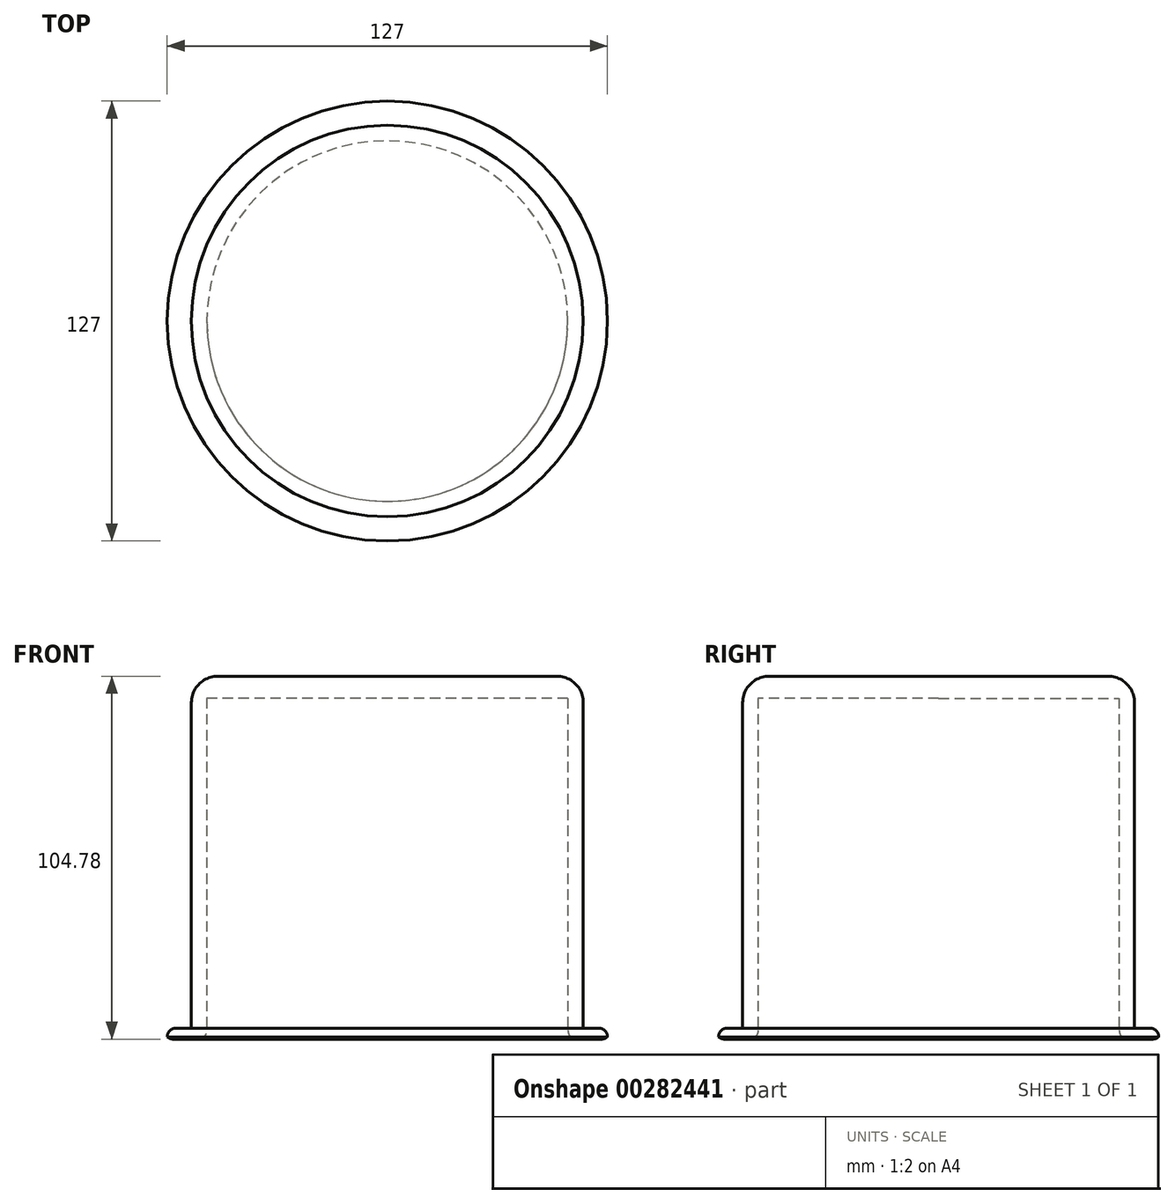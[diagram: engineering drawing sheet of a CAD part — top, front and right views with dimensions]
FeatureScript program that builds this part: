
annotation { "Feature Type Name" : "Feature", "Feature Type Description" : "" }
export const myFeature = defineFeature(function(context is Context, id is Id, definition is map)
    precondition{}
    {
        {
            var Q0;
            Q0=qCreatedBy(makeId("Top.planeOp"),FACE);
            var sketch = newSketch(context, id + "F0", { "sketchPlane" : qUnion([Q0])});
            skCircle(sketch, "E0", {"center": v(0, 0) * mm, "radius": 56.52 * mm});
            skSolve(sketch);
        }
        {
            var Q0;
            Q0=makeQuery(id+"F0.imprint","IMPRINT",FACE,{"disambiguationData":[TD([[makeQuery(id+"F0.imprint","IMPRINT",EDGE,{"derivedFrom":sQuery(id+"F0.wireOp",EDGE,"E0")}),1.0]])]});
            extrude(context, id + "F1", {"entities" : qUnion([Q0]), "depth" : 101.6 * mm});
        }
        {
            var Q0;
            Q0=qCreatedBy(makeId("Top.planeOp"),FACE);
            var sketch = newSketch(context, id + "F2", { "sketchPlane" : qUnion([Q0])});
            skCircle(sketch, "E1", {"center": v(0, 0) * mm, "radius": 52.07 * mm});
            skSolve(sketch);
        }
        {
            var Q0;
            Q0=qSketchRegion(id+"F2",true);
            extrude(context, id + "F3", {"entities" : qUnion([Q0]), "operationType" : NewBodyOperationType.REMOVE, "depth" : 95.25 * mm});
        }
        {
            var Q0;
            Q0=makeQuery(id+"F1.opExtrude","CAP_FACE",FACE,{"disambiguationData":[OSD([sQuery(id+"F0.wireOp",EDGE,"E0")])],"isStart":true});
            var sketch = newSketch(context, id + "F4", { "sketchPlane" : qUnion([Q0])});
            skCircle(sketch, "E2", {"center": v(0, 0) * mm, "radius": 63.5 * mm});
            skLineSegment(sketch, "E3", {"start": v(34.77, -38.76) * mm, "end": v(41.13, -38.76) * mm, "construction": true});
            skSolve(sketch);
        }
        {
            var Q0;
            Q0=qSketchRegion(id+"F4",true);
            extrude(context, id + "F5", {"entities" : qUnion([Q0]), "operationType" : NewBodyOperationType.ADD, "depth" : 3.17 * mm});
        }
        {
            var Q0;
            Q0=qCreatedBy(makeId("Top.planeOp"),FACE);
            var sketch = newSketch(context, id + "F6", { "sketchPlane" : qUnion([Q0])});
            skCircle(sketch, "E4", {"center": v(0, 0) * mm, "radius": 52.07 * mm});
            skSolve(sketch);
        }
        {
            var Q0;
            Q0=qSketchRegion(id+"F6",true);
            extrude(context, id + "F7", {"entities" : qUnion([Q0]), "operationType" : NewBodyOperationType.REMOVE, "oppositeDirection" : true, "depth" : 12.7 * mm});
        }
        {
            var Q0;
            Q0=makeQuery(id+"F1.opExtrude","CAP_EDGE",EDGE,{"disambiguationData":[OSD([sQuery(id+"F0.wireOp",EDGE,"E0")])],"isStart":false});
            fillet(context, id + "F8", {"entities" : qUnion([Q0]), "radius" : 7.62 * mm, "tangentPropagation" : true, "allowEdgeOverflow" : false});
        }
        {
            var Q0;
            Q0=makeQuery(id+"F7.boolean.opBoolean","INTERSECT",EDGE,{"derivedFrom":[makeQuery(id+"F5.opExtrude","CAP_FACE",FACE,{"disambiguationData":[OSD([sQuery(id+"F4.wireOp",EDGE,"E2")])],"isStart":false}),makeQuery(id+"F7.opExtrude","SWEPT_FACE",FACE,{"disambiguationData":[OSD([sQuery(id+"F6.wireOp",EDGE,"E4")])]})]});
            fillet(context, id + "F9", {"entities" : qUnion([Q0]), "radius" : 2.54 * mm, "tangentPropagation" : true, "allowEdgeOverflow" : false});
        }
        {
            var Q0;
            Q0=makeQuery(id+"F5.opExtrude","CAP_EDGE",EDGE,{"disambiguationData":[OSD([sQuery(id+"F4.wireOp",EDGE,"E2")])],"isStart":true});
            fillet(context, id + "F10", {"entities" : qUnion([Q0]), "radius" : 2.54 * mm, "tangentPropagation" : true, "allowEdgeOverflow" : false});
        }
        {
            var Q0;
            Q0=makeQuery(id+"F5.opExtrude","CAP_EDGE",EDGE,{"disambiguationData":[OSD([sQuery(id+"F4.wireOp",EDGE,"E2")])],"isStart":false});
            fillet(context, id + "F11", {"entities" : qUnion([Q0]), "radius" : 2.54 * mm, "tangentPropagation" : true, "allowEdgeOverflow" : false});
        }
    });
